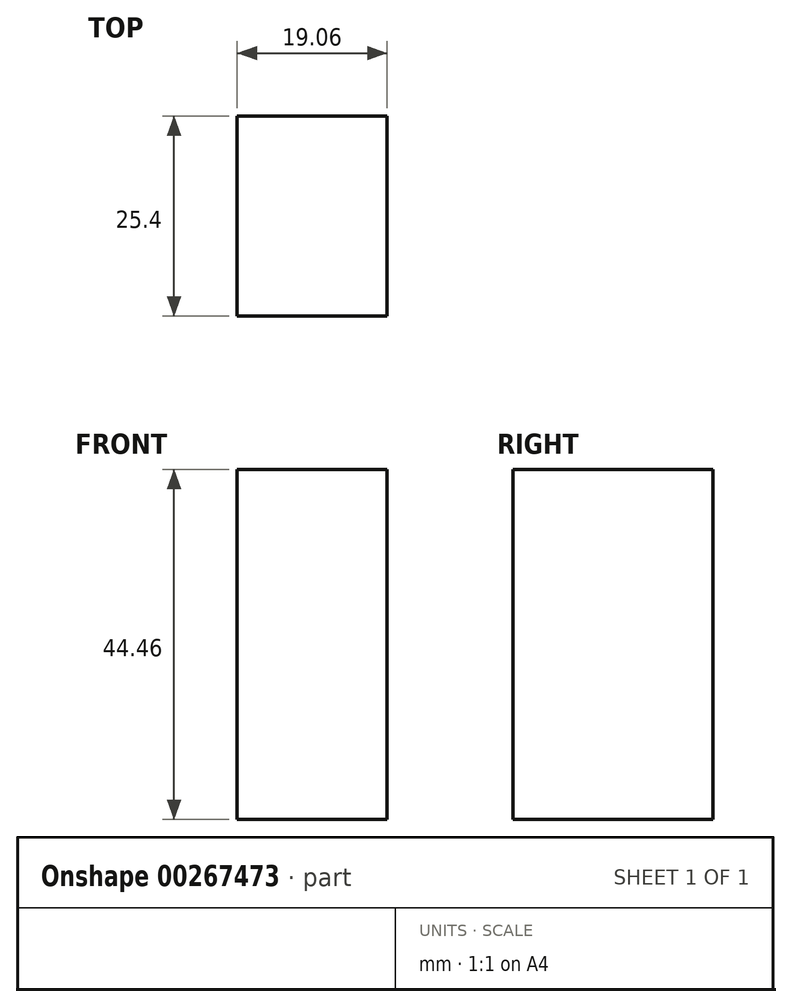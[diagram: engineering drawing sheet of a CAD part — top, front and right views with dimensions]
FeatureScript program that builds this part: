
annotation { "Feature Type Name" : "Feature", "Feature Type Description" : "" }
export const myFeature = defineFeature(function(context is Context, id is Id, definition is map)
    precondition{}
    {
        {
            var Q0;
            Q0=qCreatedBy(makeId("Front.planeOp"),FACE);
            var sketch = newSketch(context, id + "F0", { "sketchPlane" : qUnion([Q0])});
            skLineSegment(sketch, "E0.bottom", {"start": v(-9.52, 22.23) * mm, "end": v(9.53, 22.23) * mm});
            skLineSegment(sketch, "E0.top", {"start": v(-9.53, -22.23) * mm, "end": v(9.52, -22.23) * mm});
            skLineSegment(sketch, "E0.left", {"start": v(-9.52, 22.23) * mm, "end": v(-9.53, -22.23) * mm});
            skLineSegment(sketch, "E0.right", {"start": v(9.53, 22.23) * mm, "end": v(9.52, -22.23) * mm});
            skPoint(sketch, "E0.middle", {"position": v(0, 0) * mm});
            skSolve(sketch);
        }
        {
            var Q0;
            Q0 = qSketchRegion(id + "F0", true);
            extrude(context, id + "F1", {"entities" : qUnion([Q0]), "depth" : 25.4 * mm});
        }
    });
